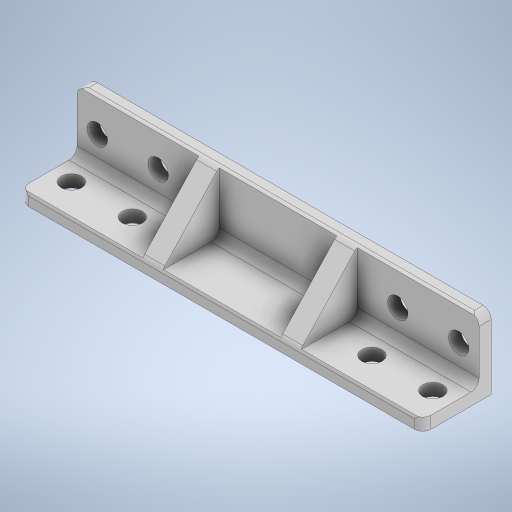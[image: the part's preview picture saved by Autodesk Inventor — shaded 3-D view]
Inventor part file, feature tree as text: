
AUTODESK INVENTOR PART (.ipt)
format: ipt  version: 2024.3 (Build 283343000, 343)  size: 340,480 bytes
history: native  units: mm
features: sketch x6, extrude x4, hole x2, other x1, fillet x1, projected_geometry x1
ambient origin geometry x8: Origin, YZ Plane, XZ Plane, XY Plane, X Axis, Y Axis, Z Axis, Center Point
bodies: Body1 (feature_tree)
feature tree (15):
  other  "ソリッド1"
  extrude  "押し出し1"  Depth=3.0mm
  extrude  "押し出し2"  Depth=99.0mm
  hole  "穴1"  [1 undecoded]
  hole  "穴2"  [1 undecoded]
  extrude  "押し出し5"  Depth=15.0mm TaperAngle=0.0deg
  extrude  "押し出し6"  Depth=15.0mm
  fillet  "フィレット1"  Radius=6.4mm
  sketch  "スケッチ1"
  sketch  "スケッチ2"
  sketch  "スケッチ3"
  sketch  "スケッチ4"
  sketch  "スケッチ7"
  sketch  "スケッチ8"
  projected_geometry  "投影ループ3"
note: 2 required parameter values undecoded (feature->parameter linkage not recoverable at this tier; creation-order binding heuristic only, values carry confidence <= 0.55)
